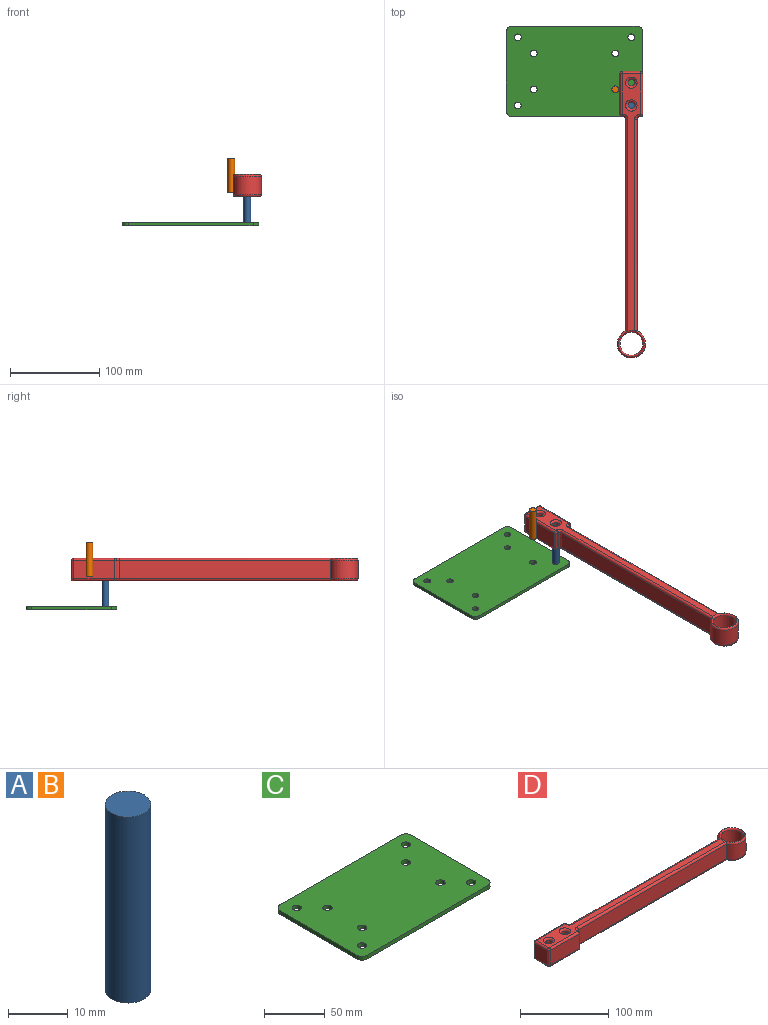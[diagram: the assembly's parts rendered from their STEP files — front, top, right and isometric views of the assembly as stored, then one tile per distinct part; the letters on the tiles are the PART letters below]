
ASSEMBLY  parts=4 mates=3
PART A: 3 faces, bbox 7.6x7.6x38.1 mm
  f0: cylinder r=3.81mm len=38.1mm, axis (0,0,-1), area 912.1mm2, adj f1,f2
  f1: plane 7.62x7.62mm, normal (0,0,1), area 45.6mm2, adj f0
  f2: plane 7.62x7.62mm, normal (0,0,-1), area 45.6mm2, adj f0
PART B: same geometry as A
PART C: 18 faces, bbox 152.4x101.6x3.8 mm
  f0: plane 152.4x101.6mm, normal (0,0,1), area 15084.4mm2, adj f2,f3,f4,f5,f6,f7,f8,f9
  f1: plane 152.4x101.6mm, normal (0,0,-1), area 15084.4mm2, adj f2,f3,f4,f5,f6,f7,f8,f9
  f2: plane 139.7x3.81mm, normal (0,-1,0), area 532.3mm2, adj f0,f1,f3,f9
  f3: cylinder r=6.35mm len=6.35mm, axis (0,0,-1), area 38mm2, adj f0,f1,f2,f4
  f4: plane 88.9x3.81mm, normal (1,0,0), area 338.7mm2, adj f0,f1,f3,f5
  f5: cylinder r=6.35mm len=6.35mm, axis (0,0,-1), area 38mm2, adj f0,f1,f4,f6
  f6: plane 139.7x3.81mm, normal (0,1,0), area 532.3mm2, adj f0,f1,f5,f7
  f7: cylinder r=6.35mm len=6.35mm, axis (0,0,-1), area 38mm2, adj f0,f1,f6,f8
  f8: plane 88.9x3.81mm, normal (-1,0,0), area 338.7mm2, adj f0,f1,f7,f9
  f9: cylinder r=6.35mm len=6.35mm, axis (0,0,-1), area 38mm2, adj f0,f1,f2,f8
  f10: cylinder r=3.81mm len=7.62mm, axis (0,0,1), area 91.2mm2, adj f0,f1
  f11: cylinder r=3.81mm len=7.62mm, axis (0,0,1), area 91.2mm2, adj f0,f1
  f12: cylinder r=3.81mm len=7.62mm, axis (0,0,1), area 91.2mm2, adj f0,f1
  f13: cylinder r=3.81mm len=7.62mm, axis (0,0,1), area 91.2mm2, adj f0,f1
  f14: cylinder r=3.81mm len=7.62mm, axis (0,0,1), area 91.2mm2, adj f0,f1
  f15: cylinder r=3.81mm len=7.62mm, axis (0,0,1), area 91.2mm2, adj f0,f1
  f16: cylinder r=3.81mm len=7.62mm, axis (0,0,1), area 91.2mm2, adj f0,f1
  f17: cylinder r=3.81mm len=7.62mm, axis (0,0,1), area 91.2mm2, adj f0,f1
PART D: 53 faces, bbox 323.2x36.9x25.4 mm
  f0: plane 236.83x20.32mm, normal (0,1,0), area 4812.4mm2, adj f9,f42,f45,f48
  f1: plane 20.32x1.27mm, normal (1,0,0), area 25.8mm2, adj f33,f43,f44,f48
  f2: plane 45.72x20.32mm, normal (0,1,0), area 929mm2, adj f23,f32,f33,f34
  f3: plane 20.32x20.32mm, normal (-1,0,0), area 412.9mm2, adj f14,f22,f23,f24
  f4: plane 45.72x20.32mm, normal (0,-1,0), area 929mm2, adj f13,f14,f15,f16
  f5: plane 20.32x1.27mm, normal (1,0,0), area 25.8mm2, adj f16,f21,f25,f26
  f6: plane 236.83x20.32mm, normal (0,-1,0), area 4812.4mm2, adj f9,f26,f31,f35
  f7: cylinder r=3.81mm len=20.32mm, axis (0,0,-1), area 486.4mm2, adj f49,f51
  f8: cylinder r=12.7mm len=25.4mm, axis (0,0,-1), area 1621.5mm2, adj f37,f40
  f9: cylinder r=15.88mm len=31.75mm, axis (0,0,-1), area 1761.3mm2, adj f0,f6,f36,f41
  f10: cylinder r=3.81mm len=20.32mm, axis (0,0,-1), area 486.4mm2, adj f50,f52
  f11: plane 287.42x20.32mm, normal (0,0,1), area 2526.1mm2, adj f13,f21,f22,f27,f31,f32,f37,f42
  f12: plane 287.42x20.32mm, normal (0,0,-1), area 2526.1mm2, adj f15,f24,f25,f30,f34,f35,f40,f44
  f13: cylinder r=2.54mm len=45.72mm, axis (-1,0,0), area 182.4mm2, adj f4,f11,f17,f18
  f14: cylinder r=2.54mm len=20.32mm, axis (0,0,-1), area 81.1mm2, adj f3,f4,f18,f19
  f15: cylinder r=2.54mm len=45.72mm, axis (1,0,0), area 182.4mm2, adj f4,f12,f19,f20
  f16: cylinder r=2.54mm len=20.32mm, axis (0,0,1), area 81.1mm2, adj f4,f5,f17,f20
  f17: sphere r=2.54mm, area 10.1mm2, adj f13,f16,f21
  f18: sphere r=2.54mm, area 10.1mm2, adj f13,f14,f22
  f19: sphere r=2.54mm, area 10.1mm2, adj f14,f15,f24
  f20: sphere r=2.54mm, area 10.1mm2, adj f15,f16,f25
  f21: cylinder r=2.54mm len=2.54mm, axis (0,-1,0), area 5.1mm2, adj f5,f11,f17,f27
  f22: cylinder r=2.54mm len=20.32mm, axis (0,1,0), area 81.1mm2, adj f3,f11,f18,f28
  f23: cylinder r=2.54mm len=20.32mm, axis (0,0,1), area 81.1mm2, adj f2,f3,f28,f29
  f24: cylinder r=2.54mm len=20.32mm, axis (0,-1,0), area 81.1mm2, adj f3,f12,f19,f29
  f25: cylinder r=2.54mm len=2.54mm, axis (0,1,0), area 5.1mm2, adj f5,f12,f20,f30
  f26: cylinder r=2.54mm len=20.32mm, axis (0,0,1), area 81.1mm2, adj f5,f6,f27,f30
  f27: torus R=5.08mm, axis (0,0,1), area 21.7mm2, adj f11,f21,f26,f31
  f28: sphere r=2.54mm, area 10.1mm2, adj f22,f23,f32
  f29: sphere r=2.54mm, area 10.1mm2, adj f23,f24,f34
  f30: torus R=5.08mm, axis (0,0,1), area 21.7mm2, adj f12,f25,f26,f35
  f31: cylinder r=2.54mm len=237.91mm, axis (-1,0,0), area 946.5mm2, adj f6,f11,f27,f36,f37
  f32: cylinder r=2.54mm len=45.72mm, axis (1,0,0), area 182.4mm2, adj f2,f11,f28,f38
  f33: cylinder r=2.54mm len=20.32mm, axis (0,0,-1), area 81.1mm2, adj f1,f2,f38,f39
  f34: cylinder r=2.54mm len=45.72mm, axis (-1,0,0), area 182.4mm2, adj f2,f12,f29,f39
  f35: cylinder r=2.54mm len=237.91mm, axis (1,0,0), area 946.5mm2, adj f6,f12,f30,f40,f41
  f36: torus R=13.33mm, axis (0,0,1), area 254.2mm2, adj f9,f31,f37,f42
  f37: torus R=15.24mm, axis (0,0,1), area 259.5mm2, adj f8,f11,f31,f36,f42
  f38: sphere r=2.54mm, area 10.1mm2, adj f32,f33,f43
  f39: sphere r=2.54mm, area 10.1mm2, adj f33,f34,f44
  f40: torus R=15.24mm, axis (0,0,1), area 259.5mm2, adj f8,f12,f35,f41,f45
  f41: torus R=13.33mm, axis (0,0,1), area 254.2mm2, adj f9,f35,f40,f45
  f42: cylinder r=2.54mm len=237.91mm, axis (1,0,0), area 946.5mm2, adj f0,f11,f36,f37,f46
  f43: cylinder r=2.54mm len=2.54mm, axis (0,-1,0), area 5.1mm2, adj f1,f11,f38,f46
  f44: cylinder r=2.54mm len=2.54mm, axis (0,1,0), area 5.1mm2, adj f1,f12,f39,f47
  f45: cylinder r=2.54mm len=237.91mm, axis (-1,0,0), area 946.5mm2, adj f0,f12,f40,f41,f47
  f46: torus R=5.08mm, axis (0,0,1), area 21.7mm2, adj f11,f42,f43,f48
  f47: torus R=5.08mm, axis (0,0,1), area 21.7mm2, adj f12,f44,f45,f48
  f48: cylinder r=2.54mm len=20.32mm, axis (0,0,-1), area 81.1mm2, adj f0,f1,f46,f47
  f49: torus R=6.35mm, axis (0,0,1), area 118.7mm2, adj f7,f12
  f50: torus R=6.35mm, axis (0,0,1), area 118.7mm2, adj f10,f12
  f51: torus R=6.35mm, axis (0,0,1), area 118.7mm2, adj f7,f11
  f52: torus R=6.35mm, axis (0,0,1), area 118.7mm2, adj f10,f11
PLACE A rot(axis=(0,0,1),180deg) t=(-196.36,349.26,10.15)mm
PLACE B rot(axis=(0,0,1),180deg) t=(-214.32,367.22,44.82)mm
PLACE C rot(axis=(0,0,1),180deg) t=(-336.06,438.16,6.98)mm fixed
PLACE D rot(axis=(0,0,-1),90deg) t=(-202.71,336.56,39.41)mm
MATE slider C.f13 <-> B.f0  axis (0,0,1) through (-214.32,367.22,10.79)mm
MATE slider A.f0 <-> C.f14  axis (0,0,-1) through (-196.36,349.26,48.25)mm
MATE slider A.f0 <-> D.f10  axis (0,0,1) through (-196.36,349.26,48.25)mm
